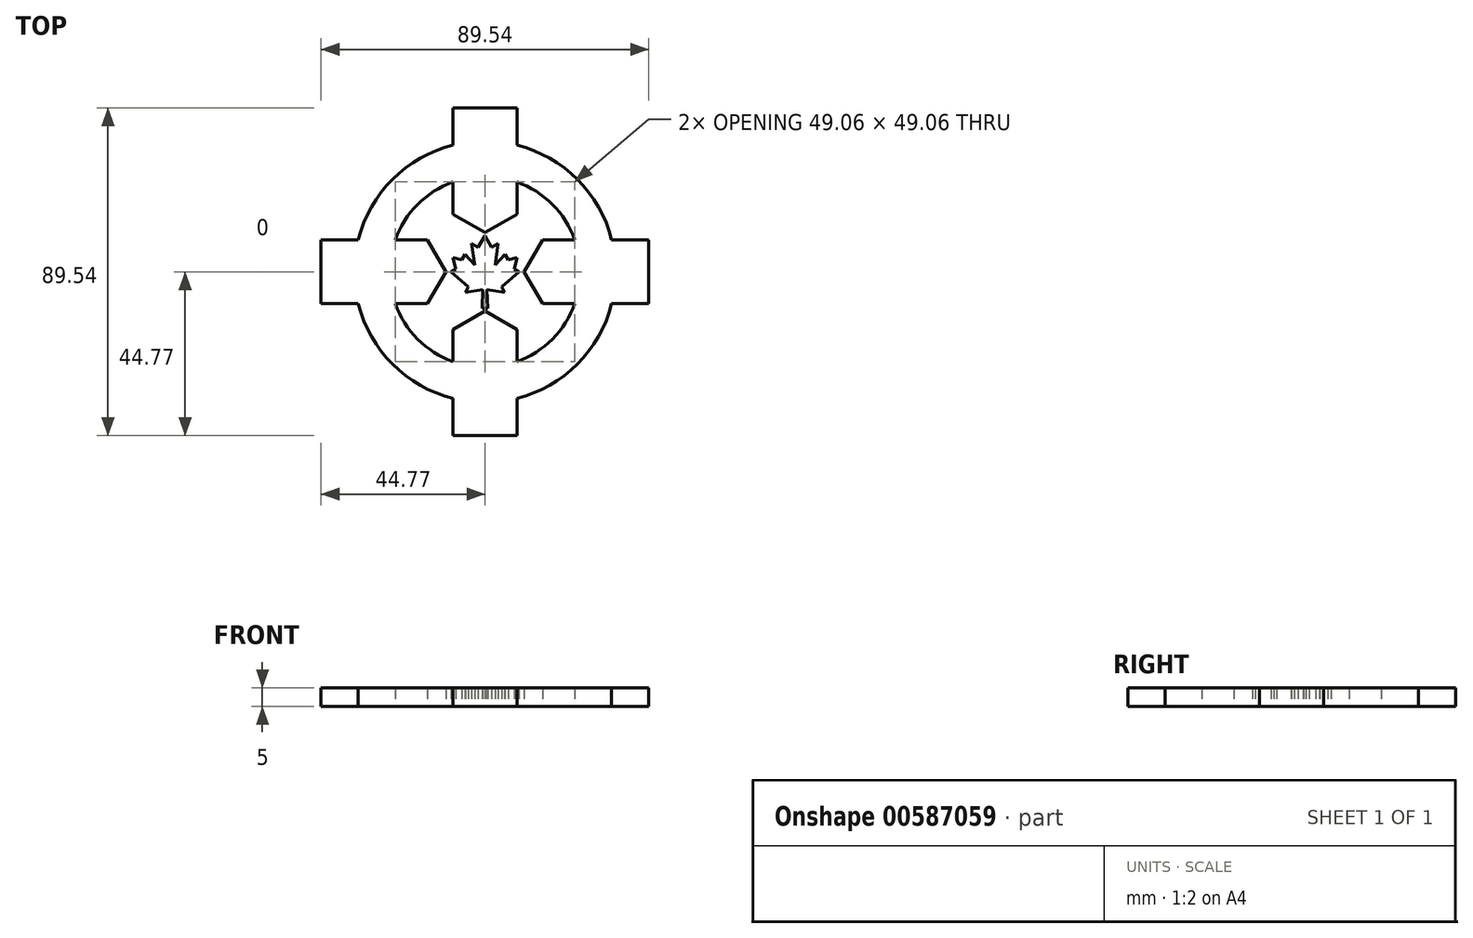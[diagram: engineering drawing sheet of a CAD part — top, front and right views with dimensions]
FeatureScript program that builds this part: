
annotation { "Feature Type Name" : "Feature", "Feature Type Description" : "" }
export const myFeature = defineFeature(function(context is Context, id is Id, definition is map)
    precondition{}
    {
        {
            var Q0;
            Q0=qCreatedBy(makeId("Top.planeOp"),FACE);
            var sketch = newSketch(context, id + "F0", { "sketchPlane" : qUnion([Q0])});
            skLineSegment(sketch, "E0", {"start": v(-44.77, 0) * mm, "end": v(-44.77, 8.73) * mm});
            skLineSegment(sketch, "E1", {"start": v(-44.77, 8.73) * mm, "end": v(-15.75, 8.73) * mm});
            skLineSegment(sketch, "E2", {"start": v(-15.75, 8.73) * mm, "end": v(-10.72, 0) * mm});
            skLineSegment(sketch, "E3", {"start": v(-44.77, 0) * mm, "end": v(-10.72, 0) * mm});
            skLineSegment(sketch, "E4.MirrorCS", {"start": v(-44.77, 0) * mm, "end": v(-44.77, -8.73) * mm});
            skLineSegment(sketch, "E5.MirrorCS", {"start": v(-44.77, -8.73) * mm, "end": v(-15.75, -8.73) * mm});
            skLineSegment(sketch, "E6.MirrorCS", {"start": v(-15.75, -8.73) * mm, "end": v(-10.72, 0) * mm});
            skLineSegment(sketch, "E7.1.0", {"start": v(0, -44.77) * mm, "end": v(0, -10.72) * mm});
            skLineSegment(sketch, "E7.1.1", {"start": v(-8.73, -15.75) * mm, "end": v(0, -10.72) * mm});
            skLineSegment(sketch, "E7.1.2", {"start": v(-8.73, -44.77) * mm, "end": v(-8.73, -15.75) * mm});
            skLineSegment(sketch, "E7.1.3", {"start": v(8.73, -15.75) * mm, "end": v(0, -10.72) * mm});
            skLineSegment(sketch, "E7.1.4", {"start": v(8.73, -44.77) * mm, "end": v(8.73, -15.75) * mm});
            skLineSegment(sketch, "E7.1.5", {"start": v(0, -44.77) * mm, "end": v(-8.73, -44.77) * mm});
            skLineSegment(sketch, "E7.1.6", {"start": v(0, -44.77) * mm, "end": v(8.73, -44.77) * mm});
            skLineSegment(sketch, "E7.2.0", {"start": v(44.77, 0) * mm, "end": v(10.72, 0) * mm});
            skLineSegment(sketch, "E7.2.1", {"start": v(15.75, -8.73) * mm, "end": v(10.72, 0) * mm});
            skLineSegment(sketch, "E7.2.2", {"start": v(44.77, -8.73) * mm, "end": v(15.75, -8.73) * mm});
            skLineSegment(sketch, "E7.2.3", {"start": v(15.75, 8.73) * mm, "end": v(10.72, 0) * mm});
            skLineSegment(sketch, "E7.2.4", {"start": v(44.77, 8.73) * mm, "end": v(15.75, 8.73) * mm});
            skLineSegment(sketch, "E7.2.5", {"start": v(44.77, 0) * mm, "end": v(44.77, -8.73) * mm});
            skLineSegment(sketch, "E7.2.6", {"start": v(44.77, 0) * mm, "end": v(44.77, 8.73) * mm});
            skLineSegment(sketch, "E7.3.0", {"start": v(0, 44.77) * mm, "end": v(0, 10.72) * mm});
            skLineSegment(sketch, "E7.3.1", {"start": v(8.73, 15.75) * mm, "end": v(0, 10.72) * mm});
            skLineSegment(sketch, "E7.3.2", {"start": v(8.73, 44.77) * mm, "end": v(8.73, 15.75) * mm});
            skLineSegment(sketch, "E7.3.3", {"start": v(-8.73, 15.75) * mm, "end": v(0, 10.72) * mm});
            skLineSegment(sketch, "E7.3.4", {"start": v(-8.73, 44.77) * mm, "end": v(-8.73, 15.75) * mm});
            skLineSegment(sketch, "E7.3.5", {"start": v(0, 44.77) * mm, "end": v(8.73, 44.77) * mm});
            skLineSegment(sketch, "E7.3.6", {"start": v(0, 44.77) * mm, "end": v(-8.73, 44.77) * mm});
            skPoint(sketch, "E7.center", {"position": v(0, 0) * mm});
            skLineSegment(sketch, "E8", {"start": v(0, 0) * mm, "end": v(0, 9.9) * mm});
            skLineSegment(sketch, "E9", {"start": v(0, 9.9) * mm, "end": v(-1.88, 6.64) * mm});
            skLineSegment(sketch, "E10", {"start": v(-1.88, 6.64) * mm, "end": v(-3.65, 7.66) * mm});
            skLineSegment(sketch, "E11", {"start": v(-3.65, 7.66) * mm, "end": v(-2.84, 1.8) * mm});
            skLineSegment(sketch, "E12", {"start": v(-2.84, 1.8) * mm, "end": v(-5.44, 4.76) * mm});
            skLineSegment(sketch, "E13", {"start": v(-5.44, 4.76) * mm, "end": v(-6.34, 3.2) * mm});
            skLineSegment(sketch, "E14", {"start": v(-6.34, 3.2) * mm, "end": v(-8.77, 3.86) * mm});
            skLineSegment(sketch, "E15", {"start": v(-8.77, 3.86) * mm, "end": v(-7.98, 0.74) * mm});
            skLineSegment(sketch, "E16", {"start": v(-7.98, 0.74) * mm, "end": v(-9.25, -0.11) * mm});
            skLineSegment(sketch, "E17", {"start": v(-9.25, -0.11) * mm, "end": v(-4.59, -4.08) * mm});
            skLineSegment(sketch, "E18", {"start": v(-4.59, -4.08) * mm, "end": v(-5.33, -5.67) * mm});
            skLineSegment(sketch, "E19", {"start": v(-5.33, -5.67) * mm, "end": v(-0.56, -4.88) * mm});
            skLineSegment(sketch, "E20", {"start": v(-0.56, -4.88) * mm, "end": v(-0.78, -9.96) * mm});
            skLineSegment(sketch, "E21", {"start": v(-0.78, -9.96) * mm, "end": v(0.02, -9.91) * mm});
            skLineSegment(sketch, "E22", {"start": v(0.02, -9.91) * mm, "end": v(0, 0) * mm});
            skLineSegment(sketch, "E23.MirrorCS", {"start": v(0.58, -4.88) * mm, "end": v(0.81, -9.96) * mm});
            skLineSegment(sketch, "E24.MirrorCS", {"start": v(0.81, -9.96) * mm, "end": v(0.02, -9.91) * mm});
            skLineSegment(sketch, "E25.MirrorCS", {"start": v(5.35, -5.65) * mm, "end": v(0.58, -4.88) * mm});
            skLineSegment(sketch, "E26.MirrorCS", {"start": v(4.6, -4.07) * mm, "end": v(5.35, -5.65) * mm});
            skLineSegment(sketch, "E27.MirrorCS", {"start": v(9.25, -0.08) * mm, "end": v(4.6, -4.07) * mm});
            skLineSegment(sketch, "E28.MirrorCS", {"start": v(7.98, 0.77) * mm, "end": v(9.25, -0.08) * mm});
            skLineSegment(sketch, "E29.MirrorCS", {"start": v(8.76, 3.9) * mm, "end": v(7.98, 0.77) * mm});
            skLineSegment(sketch, "E30.MirrorCS", {"start": v(6.32, 3.23) * mm, "end": v(8.76, 3.9) * mm});
            skLineSegment(sketch, "E31.MirrorCS", {"start": v(5.42, 4.78) * mm, "end": v(6.32, 3.23) * mm});
            skLineSegment(sketch, "E32.MirrorCS", {"start": v(2.83, 1.8) * mm, "end": v(5.42, 4.78) * mm});
            skLineSegment(sketch, "E33.MirrorCS", {"start": v(3.62, 7.67) * mm, "end": v(2.83, 1.8) * mm});
            skLineSegment(sketch, "E34.MirrorCS", {"start": v(1.86, 6.64) * mm, "end": v(3.62, 7.67) * mm});
            skLineSegment(sketch, "E35.MirrorCS", {"start": v(-0.04, 9.9) * mm, "end": v(1.86, 6.64) * mm});
            skCircle(sketch, "E36", {"center": v(0, 0) * mm, "radius": 26.04 * mm});
            skCircle(sketch, "E37", {"center": v(0, 0) * mm, "radius": 35.7 * mm});
            skSolve(sketch);
        }
        {
            var Q0;
            {var subQ0=sQuery(id+"F0.wireOp",EDGE,"E7.3.6");Q0=makeQuery(id+"F0.imprint","IMPRINT",FACE,{"disambiguationData":[TD([[makeQuery(id+"F0.imprint","IMPRINT",EDGE,{"derivedFrom":subQ0}),1.0]])]});}
            var Q1;
            {var subQ0=sQuery(id+"F0.wireOp",EDGE,"E7.3.5");Q1=makeQuery(id+"F0.imprint","IMPRINT",FACE,{"disambiguationData":[TD([[makeQuery(id+"F0.imprint","IMPRINT",EDGE,{"derivedFrom":subQ0}),-1.0]])]});}
            var Q2;
            {var subQ0=sQuery(id+"F0.wireOp",EDGE,"E37");var subQ1=sQuery(id+"F0.wireOp",EDGE,"E7.3.0");var subQ2=makeQuery(id+"F0.imprint","INTERSECT",VERTEX,{"derivedFrom":[subQ1,subQ0]});Q2=makeQuery(id+"F0.imprint","IMPRINT",FACE,{"disambiguationData":[TD([[makeQuery(id+"F0.imprint","IMPRINT",EDGE,{"disambiguationData":[TD([[subQ2,-1.0]])],"derivedFrom":subQ1}),1.0]])]});}
            var Q3;
            {var subQ0=sQuery(id+"F0.wireOp",EDGE,"E37");var subQ1=sQuery(id+"F0.wireOp",EDGE,"E7.3.0");var subQ2=makeQuery(id+"F0.imprint","INTERSECT",VERTEX,{"derivedFrom":[subQ1,subQ0]});Q3=makeQuery(id+"F0.imprint","IMPRINT",FACE,{"disambiguationData":[TD([[makeQuery(id+"F0.imprint","IMPRINT",EDGE,{"disambiguationData":[TD([[subQ2,-1.0]])],"derivedFrom":subQ1}),-1.0]])]});}
            var Q4;
            {var subQ0=sQuery(id+"F0.wireOp",EDGE,"E7.3.3");Q4=makeQuery(id+"F0.imprint","IMPRINT",FACE,{"disambiguationData":[TD([[makeQuery(id+"F0.imprint","IMPRINT",EDGE,{"derivedFrom":subQ0}),1.0]])]});}
            var Q5;
            {var subQ0=sQuery(id+"F0.wireOp",EDGE,"E7.3.1");Q5=makeQuery(id+"F0.imprint","IMPRINT",FACE,{"disambiguationData":[TD([[makeQuery(id+"F0.imprint","IMPRINT",EDGE,{"derivedFrom":subQ0}),-1.0]])]});}
            var Q6;
            {var subQ6=sQuery(id+"F0.wireOp",EDGE,"E10");Q6=makeQuery(id+"F0.imprint","IMPRINT",FACE,{"disambiguationData":[TD([[makeQuery(id+"F0.imprint","IMPRINT",EDGE,{"derivedFrom":subQ6}),1.0]])]});}
            var Q7;
            {var subQ0=sQuery(id+"F0.wireOp",EDGE,"E22");Q7=makeQuery(id+"F0.imprint","IMPRINT",FACE,{"disambiguationData":[TD([[makeQuery(id+"F0.imprint","IMPRINT",EDGE,{"derivedFrom":subQ0}),-1.0]])]});}
            var Q8;
            {var subQ0=sQuery(id+"F0.wireOp",EDGE,"E7.2.1");Q8=makeQuery(id+"F0.imprint","IMPRINT",FACE,{"disambiguationData":[TD([[makeQuery(id+"F0.imprint","IMPRINT",EDGE,{"derivedFrom":subQ0}),-1.0]])]});}
            var Q9;
            {var subQ0=sQuery(id+"F0.wireOp",EDGE,"E7.2.3");Q9=makeQuery(id+"F0.imprint","IMPRINT",FACE,{"disambiguationData":[TD([[makeQuery(id+"F0.imprint","IMPRINT",EDGE,{"derivedFrom":subQ0}),1.0]])]});}
            var Q10;
            {var subQ0=sQuery(id+"F0.wireOp",EDGE,"E37");var subQ1=sQuery(id+"F0.wireOp",EDGE,"E7.2.0");var subQ2=makeQuery(id+"F0.imprint","INTERSECT",VERTEX,{"derivedFrom":[subQ1,subQ0]});Q10=makeQuery(id+"F0.imprint","IMPRINT",FACE,{"disambiguationData":[TD([[makeQuery(id+"F0.imprint","IMPRINT",EDGE,{"disambiguationData":[TD([[subQ2,-1.0]])],"derivedFrom":subQ1}),-1.0]])]});}
            var Q11;
            {var subQ0=sQuery(id+"F0.wireOp",EDGE,"E37");var subQ1=sQuery(id+"F0.wireOp",EDGE,"E7.2.0");var subQ2=makeQuery(id+"F0.imprint","INTERSECT",VERTEX,{"derivedFrom":[subQ1,subQ0]});Q11=makeQuery(id+"F0.imprint","IMPRINT",FACE,{"disambiguationData":[TD([[makeQuery(id+"F0.imprint","IMPRINT",EDGE,{"disambiguationData":[TD([[subQ2,-1.0]])],"derivedFrom":subQ1}),1.0]])]});}
            var Q12;
            {var subQ0=sQuery(id+"F0.wireOp",EDGE,"E7.2.5");Q12=makeQuery(id+"F0.imprint","IMPRINT",FACE,{"disambiguationData":[TD([[makeQuery(id+"F0.imprint","IMPRINT",EDGE,{"derivedFrom":subQ0}),-1.0]])]});}
            var Q13;
            {var subQ0=sQuery(id+"F0.wireOp",EDGE,"E7.2.6");Q13=makeQuery(id+"F0.imprint","IMPRINT",FACE,{"disambiguationData":[TD([[makeQuery(id+"F0.imprint","IMPRINT",EDGE,{"derivedFrom":subQ0}),1.0]])]});}
            var Q14;
            {var subQ0=sQuery(id+"F0.wireOp",EDGE,"E37");var subQ1=sQuery(id+"F0.wireOp",EDGE,"E7.2.4");var subQ2=makeQuery(id+"F0.imprint","INTERSECT",VERTEX,{"derivedFrom":[subQ1,subQ0]});Q14=makeQuery(id+"F0.imprint","IMPRINT",FACE,{"disambiguationData":[TD([[makeQuery(id+"F0.imprint","IMPRINT",EDGE,{"disambiguationData":[TD([[subQ2,-1.0]])],"derivedFrom":subQ1}),-1.0]])]});}
            var Q15;
            {var subQ0=sQuery(id+"F0.wireOp",EDGE,"E37");var subQ1=sQuery(id+"F0.wireOp",EDGE,"E1");var subQ2=makeQuery(id+"F0.imprint","INTERSECT",VERTEX,{"derivedFrom":[subQ1,subQ0]});Q15=makeQuery(id+"F0.imprint","IMPRINT",FACE,{"disambiguationData":[TD([[makeQuery(id+"F0.imprint","IMPRINT",EDGE,{"disambiguationData":[TD([[subQ2,-1.0]])],"derivedFrom":subQ1}),1.0]])]});}
            var Q16;
            {var subQ0=sQuery(id+"F0.wireOp",EDGE,"E37");var subQ1=sQuery(id+"F0.wireOp",EDGE,"E1");var subQ2=makeQuery(id+"F0.imprint","INTERSECT",VERTEX,{"derivedFrom":[subQ1,subQ0]});Q16=makeQuery(id+"F0.imprint","IMPRINT",FACE,{"disambiguationData":[TD([[makeQuery(id+"F0.imprint","IMPRINT",EDGE,{"disambiguationData":[TD([[subQ2,-1.0]])],"derivedFrom":subQ1}),-1.0]])]});}
            var Q17;
            {var subQ0=sQuery(id+"F0.wireOp",EDGE,"E2");Q17=makeQuery(id+"F0.imprint","IMPRINT",FACE,{"disambiguationData":[TD([[makeQuery(id+"F0.imprint","IMPRINT",EDGE,{"derivedFrom":subQ0}),-1.0]])]});}
            var Q18;
            {var subQ0=sQuery(id+"F0.wireOp",EDGE,"E6.MirrorCS");Q18=makeQuery(id+"F0.imprint","IMPRINT",FACE,{"disambiguationData":[TD([[makeQuery(id+"F0.imprint","IMPRINT",EDGE,{"derivedFrom":subQ0}),1.0]])]});}
            var Q19;
            {var subQ0=sQuery(id+"F0.wireOp",EDGE,"E37");var subQ1=sQuery(id+"F0.wireOp",EDGE,"E3");var subQ2=makeQuery(id+"F0.imprint","INTERSECT",VERTEX,{"derivedFrom":[subQ1,subQ0]});Q19=makeQuery(id+"F0.imprint","IMPRINT",FACE,{"disambiguationData":[TD([[makeQuery(id+"F0.imprint","IMPRINT",EDGE,{"disambiguationData":[TD([[subQ2,-1.0]])],"derivedFrom":subQ1}),-1.0]])]});}
            var Q20;
            {var subQ0=sQuery(id+"F0.wireOp",EDGE,"E4.MirrorCS");Q20=makeQuery(id+"F0.imprint","IMPRINT",FACE,{"disambiguationData":[TD([[makeQuery(id+"F0.imprint","IMPRINT",EDGE,{"derivedFrom":subQ0}),1.0]])]});}
            var Q21;
            {var subQ0=sQuery(id+"F0.wireOp",EDGE,"E0");Q21=makeQuery(id+"F0.imprint","IMPRINT",FACE,{"disambiguationData":[TD([[makeQuery(id+"F0.imprint","IMPRINT",EDGE,{"derivedFrom":subQ0}),-1.0]])]});}
            var Q22;
            {var subQ0=sQuery(id+"F0.wireOp",EDGE,"E37");var subQ1=sQuery(id+"F0.wireOp",EDGE,"E5.MirrorCS");var subQ2=makeQuery(id+"F0.imprint","INTERSECT",VERTEX,{"derivedFrom":[subQ1,subQ0]});Q22=makeQuery(id+"F0.imprint","IMPRINT",FACE,{"disambiguationData":[TD([[makeQuery(id+"F0.imprint","IMPRINT",EDGE,{"disambiguationData":[TD([[subQ2,-1.0]])],"derivedFrom":subQ1}),-1.0]])]});}
            var Q23;
            {var subQ0=sQuery(id+"F0.wireOp",EDGE,"E37");var subQ1=sQuery(id+"F0.wireOp",EDGE,"E7.1.0");var subQ2=makeQuery(id+"F0.imprint","INTERSECT",VERTEX,{"derivedFrom":[subQ1,subQ0]});Q23=makeQuery(id+"F0.imprint","IMPRINT",FACE,{"disambiguationData":[TD([[makeQuery(id+"F0.imprint","IMPRINT",EDGE,{"disambiguationData":[TD([[subQ2,-1.0]])],"derivedFrom":subQ1}),1.0]])]});}
            var Q24;
            {var subQ0=sQuery(id+"F0.wireOp",EDGE,"E7.1.1");Q24=makeQuery(id+"F0.imprint","IMPRINT",FACE,{"disambiguationData":[TD([[makeQuery(id+"F0.imprint","IMPRINT",EDGE,{"derivedFrom":subQ0}),-1.0]])]});}
            var Q25;
            {var subQ0=sQuery(id+"F0.wireOp",EDGE,"E7.1.3");Q25=makeQuery(id+"F0.imprint","IMPRINT",FACE,{"disambiguationData":[TD([[makeQuery(id+"F0.imprint","IMPRINT",EDGE,{"derivedFrom":subQ0}),1.0]])]});}
            var Q26;
            {var subQ0=sQuery(id+"F0.wireOp",EDGE,"E37");var subQ1=sQuery(id+"F0.wireOp",EDGE,"E7.1.0");var subQ2=makeQuery(id+"F0.imprint","INTERSECT",VERTEX,{"derivedFrom":[subQ1,subQ0]});Q26=makeQuery(id+"F0.imprint","IMPRINT",FACE,{"disambiguationData":[TD([[makeQuery(id+"F0.imprint","IMPRINT",EDGE,{"disambiguationData":[TD([[subQ2,-1.0]])],"derivedFrom":subQ1}),-1.0]])]});}
            var Q27;
            {var subQ0=sQuery(id+"F0.wireOp",EDGE,"E37");var subQ1=sQuery(id+"F0.wireOp",EDGE,"E7.1.4");var subQ2=makeQuery(id+"F0.imprint","INTERSECT",VERTEX,{"derivedFrom":[subQ1,subQ0]});Q27=makeQuery(id+"F0.imprint","IMPRINT",FACE,{"disambiguationData":[TD([[makeQuery(id+"F0.imprint","IMPRINT",EDGE,{"disambiguationData":[TD([[subQ2,-1.0]])],"derivedFrom":subQ1}),-1.0]])]});}
            var Q28;
            {var subQ0=sQuery(id+"F0.wireOp",EDGE,"E7.1.6");Q28=makeQuery(id+"F0.imprint","IMPRINT",FACE,{"disambiguationData":[TD([[makeQuery(id+"F0.imprint","IMPRINT",EDGE,{"derivedFrom":subQ0}),1.0]])]});}
            var Q29;
            {var subQ0=sQuery(id+"F0.wireOp",EDGE,"E7.1.5");Q29=makeQuery(id+"F0.imprint","IMPRINT",FACE,{"disambiguationData":[TD([[makeQuery(id+"F0.imprint","IMPRINT",EDGE,{"derivedFrom":subQ0}),-1.0]])]});}
            extrude(context, id + "F1", {"entities" : qUnion([Q0, Q1, Q2, Q3, Q4, Q5, Q6, Q7, Q8, Q9, Q10, Q11, Q12, Q13, Q14, Q15, Q16, Q17, Q18, Q19, Q20, Q21, Q22, Q23, Q24, Q25, Q26, Q27, Q28, Q29]), "depth" : 5 * mm, "offsetDistance" : 25 * mm});
        }
    });
